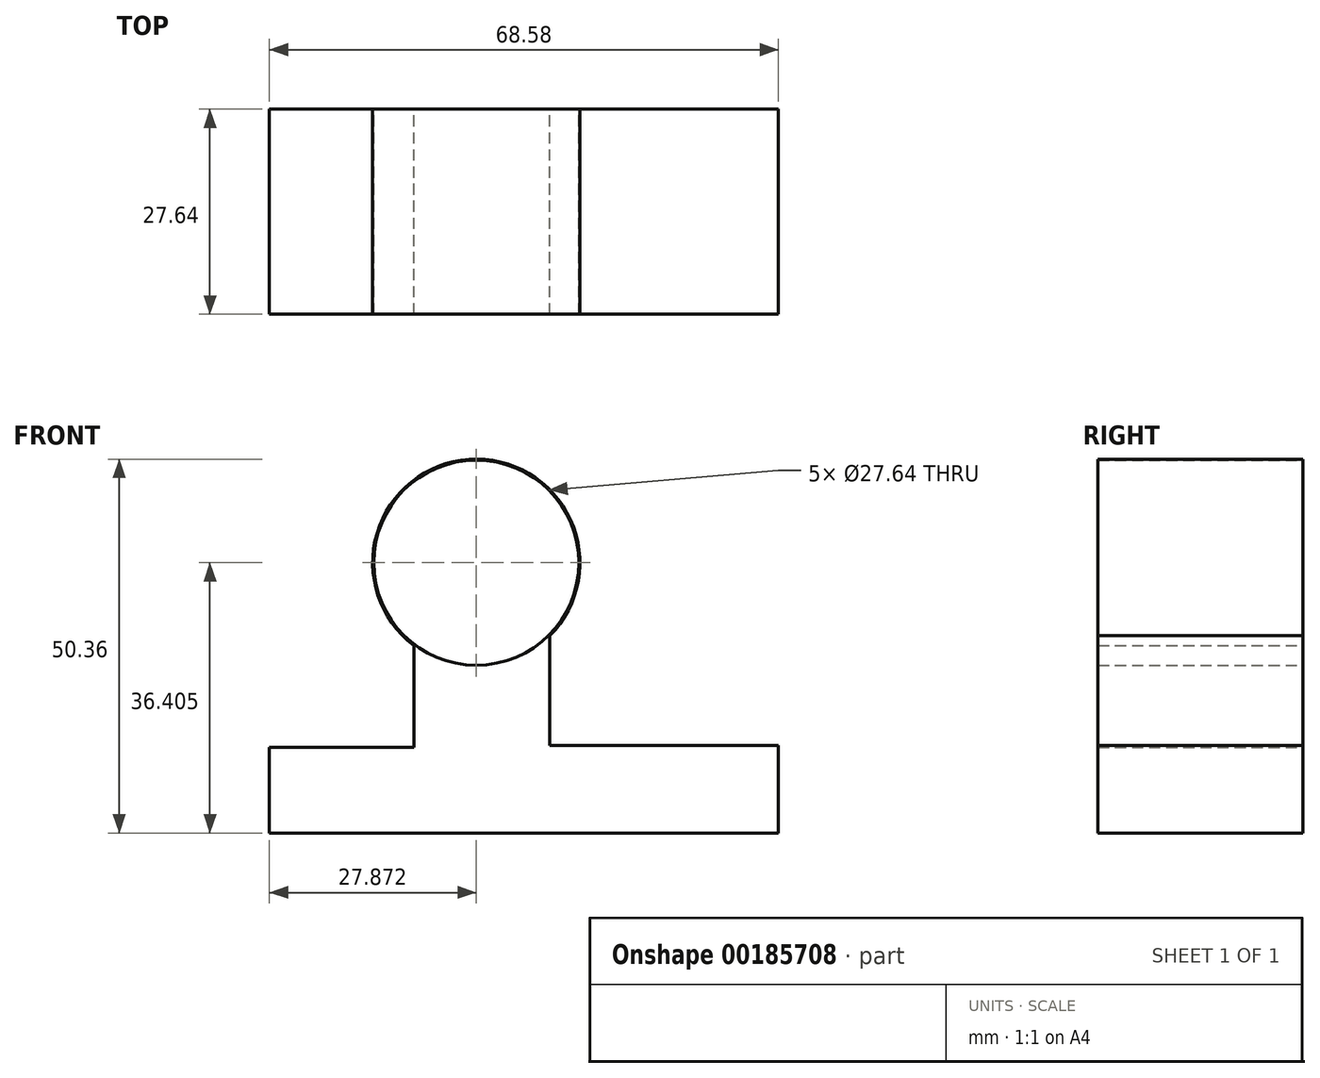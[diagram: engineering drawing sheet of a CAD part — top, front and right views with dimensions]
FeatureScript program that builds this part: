
annotation { "Feature Type Name" : "Feature", "Feature Type Description" : "" }
export const myFeature = defineFeature(function(context is Context, id is Id, definition is map)
    precondition{}
    {
        {
            var Q0;
            Q0=qCreatedBy(makeId("Front.planeOp"),FACE);
            var sketch = newSketch(context, id + "F0", { "sketchPlane" : qUnion([Q0])});
            skLineSegment(sketch, "E0", {"start": v(-31.52, -45.9) * mm, "end": v(37.06, -45.9) * mm});
            skLineSegment(sketch, "E1", {"start": v(37.06, -45.9) * mm, "end": v(37.06, -34.1) * mm});
            skLineSegment(sketch, "E2", {"start": v(37.06, -34.1) * mm, "end": v(6.25, -34.1) * mm});
            skLineSegment(sketch, "E3", {"start": v(6.25, -34.1) * mm, "end": v(6.25, -24.5) * mm});
            skLineSegment(sketch, "E4", {"start": v(-31.52, -45.9) * mm, "end": v(-31.52, -34.34) * mm});
            skLineSegment(sketch, "E5", {"start": v(-31.52, -34.34) * mm, "end": v(-12.06, -34.34) * mm});
            skLineSegment(sketch, "E6", {"start": v(-12.06, -34.34) * mm, "end": v(-12.06, -23.34) * mm});
            skCircle(sketch, "E7", {"center": v(-3.65, -9.5) * mm, "radius": 13.96 * mm});
            skCircle(sketch, "E8", {"center": v(-3.65, -9.5) * mm, "radius": 13.82 * mm});
            skLineSegment(sketch, "E9", {"start": v(6.25, -24.5) * mm, "end": v(6.25, -19.34) * mm});
            skLineSegment(sketch, "E10", {"start": v(-12.06, -23.34) * mm, "end": v(-12.06, -20.63) * mm});
            skSolve(sketch);
        }
        {
            var Q0;
            Q0 = qSketchRegion(id + "F0", true);
            extrude(context, id + "F1", {"entities" : qUnion([Q0]), "depth" : 27.64 * mm});
        }
    });
